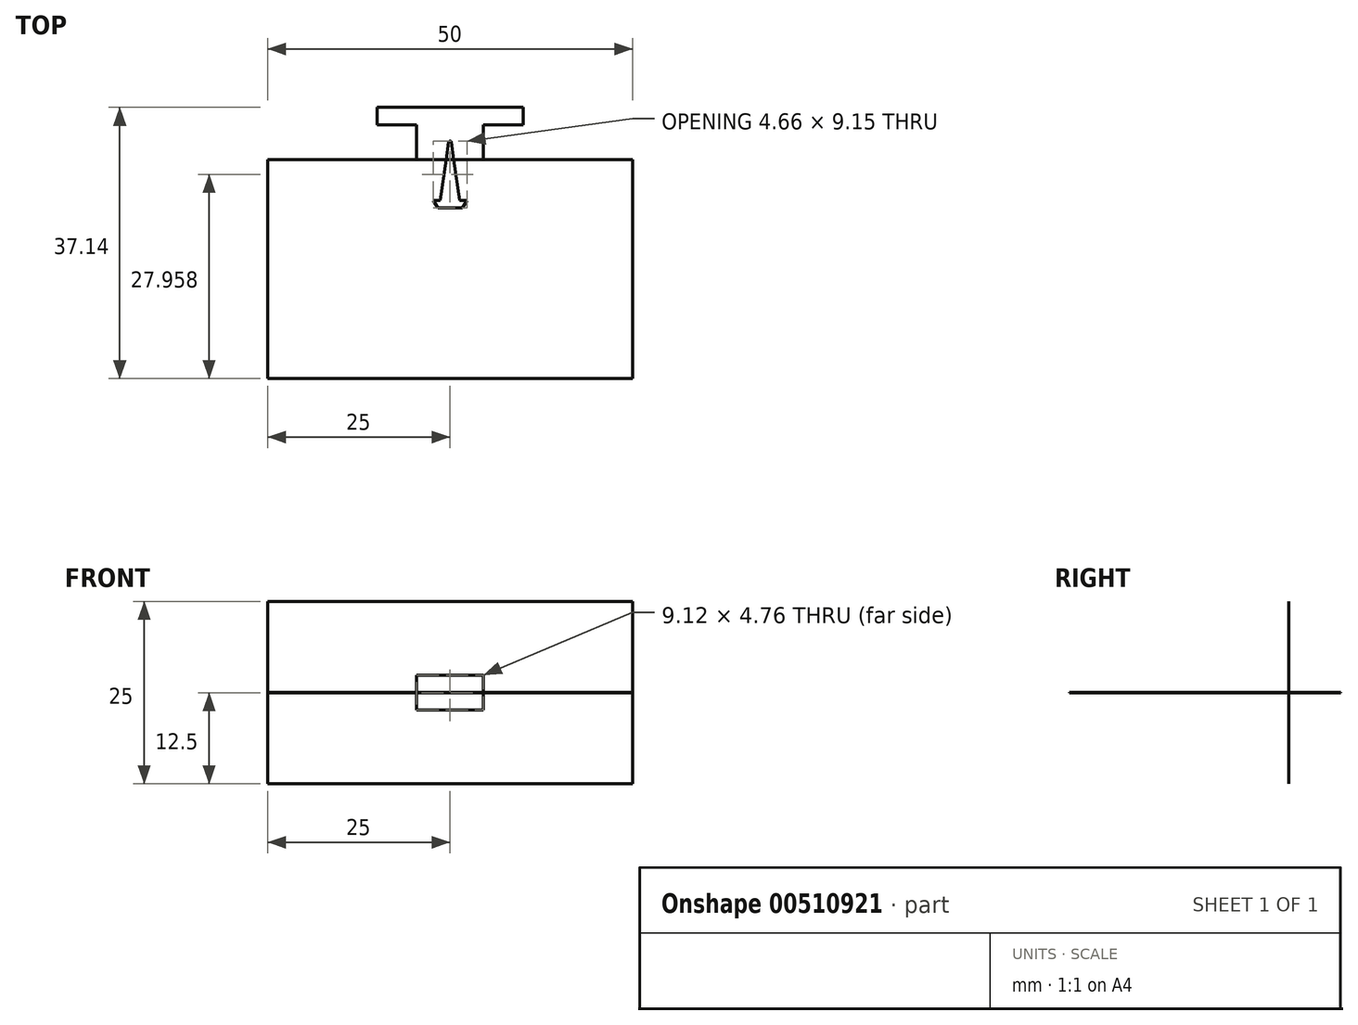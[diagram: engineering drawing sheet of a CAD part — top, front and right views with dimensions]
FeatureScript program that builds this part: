
annotation { "Feature Type Name" : "Feature", "Feature Type Description" : "" }
export const myFeature = defineFeature(function(context is Context, id is Id, definition is map)
    precondition{}
    {
        {
            assignVariable(context, id + "F0", {"name" : "thick", "anyValue" : 3 / 406.4 * mm});
        }
        {
            var Q0;
            Q0=qCreatedBy(makeId("Top.planeOp"),FACE);
            var sketch = newSketch(context, id + "F1", { "sketchPlane" : qUnion([Q0])});
            skLineSegment(sketch, "E0", {"start": v(0, 0) * mm, "end": v(0, -30) * mm, "construction": true});
            skLineSegment(sketch, "E1", {"start": v(-25, 0) * mm, "end": v(-4.56, 0) * mm});
            skLineSegment(sketch, "E2", {"start": v(-25, 0) * mm, "end": v(-25, -30) * mm});
            skLineSegment(sketch, "E3", {"start": v(-25, -30) * mm, "end": v(0, -30) * mm});
            skLineSegment(sketch, "E4.MirrorCS", {"start": v(25, -30) * mm, "end": v(0, -30) * mm});
            skLineSegment(sketch, "E5.MirrorCS", {"start": v(25, 0) * mm, "end": v(25, -30) * mm});
            skLineSegment(sketch, "E6.MirrorCS", {"start": v(25, 0) * mm, "end": v(4.56, 0) * mm});
            skLineSegment(sketch, "E7", {"start": v(4.56, 0) * mm, "end": v(4.56, 2.38) * mm});
            skLineSegment(sketch, "E8", {"start": v(4.56, 2.38) * mm, "end": v(2.18, 2.38) * mm});
            skLineSegment(sketch, "E9", {"start": v(2.18, 2.38) * mm, "end": v(2.18, -4.62) * mm});
            skLineSegment(sketch, "E10", {"start": v(2.18, -4.62) * mm, "end": v(2.98, -4.62) * mm});
            skLineSegment(sketch, "E11", {"start": v(2.98, -4.62) * mm, "end": v(1.68, -6.62) * mm});
            skLineSegment(sketch, "E12", {"start": v(1.68, -6.62) * mm, "end": v(1.68, -7.62) * mm, "construction": true});
            skLineSegment(sketch, "E13", {"start": v(1.68, -7.62) * mm, "end": v(0, -7.62) * mm, "construction": true});
            skLineSegment(sketch, "E14.MirrorCS", {"start": v(-2.18, -4.62) * mm, "end": v(-2.98, -4.62) * mm});
            skLineSegment(sketch, "E15.MirrorCS", {"start": v(-1.68, -6.62) * mm, "end": v(-1.68, -7.62) * mm, "construction": true});
            skLineSegment(sketch, "E16.MirrorCS", {"start": v(-4.56, 2.38) * mm, "end": v(-2.18, 2.38) * mm});
            skLineSegment(sketch, "E17.MirrorCS", {"start": v(-2.18, 2.38) * mm, "end": v(-2.18, -4.62) * mm});
            skLineSegment(sketch, "E18.MirrorCS", {"start": v(-4.56, 0) * mm, "end": v(-4.56, 2.38) * mm});
            skLineSegment(sketch, "E19.MirrorCS", {"start": v(-2.98, -4.62) * mm, "end": v(-1.68, -6.62) * mm});
            skLineSegment(sketch, "E20.MirrorCS", {"start": v(-1.68, -7.62) * mm, "end": v(0, -7.62) * mm, "construction": true});
            skLineSegment(sketch, "E21", {"start": v(1.68, -6.62) * mm, "end": v(-1.68, -6.62) * mm});
            skSolve(sketch);
        }
        {
            var Q0;
            Q0=makeQuery(id+"F1.imprint","IMPRINT",FACE,{"disambiguationData":[TD([[makeQuery(id+"F1.imprint","IMPRINT",EDGE,{"derivedFrom":sQuery(id+"F1.wireOp",EDGE,"E1")}),-1.0]])]});
            extrude(context, id + "F2", {"entities" : qUnion([Q0]), "endBound" : BoundingType.SYMMETRIC, "depth" : getVariable(context, 'thick')});
        }
        {
            var Q0;
            Q0=qCreatedBy(makeId("Front.planeOp"),FACE);
            var sketch = newSketch(context, id + "F3", { "sketchPlane" : qUnion([Q0])});
            skLineSegment(sketch, "E22.bottom", {"start": v(-25, 12.5) * mm, "end": v(25, 12.5) * mm});
            skLineSegment(sketch, "E22.top", {"start": v(-25, -12.5) * mm, "end": v(25, -12.5) * mm});
            skLineSegment(sketch, "E22.left", {"start": v(-25, 12.5) * mm, "end": v(-25, -12.5) * mm});
            skLineSegment(sketch, "E22.right", {"start": v(25, 12.5) * mm, "end": v(25, -12.5) * mm});
            skPoint(sketch, "E22.middle", {"position": v(0, 0) * mm});
            skLineSegment(sketch, "E23.bottom", {"start": v(4.56, 2.38) * mm, "end": v(-4.56, 2.38) * mm});
            skLineSegment(sketch, "E23.top", {"start": v(4.56, -2.38) * mm, "end": v(-4.56, -2.38) * mm});
            skLineSegment(sketch, "E23.left", {"start": v(4.56, 2.38) * mm, "end": v(4.56, -2.38) * mm});
            skLineSegment(sketch, "E23.right", {"start": v(-4.56, 2.38) * mm, "end": v(-4.56, -2.38) * mm});
            skSolve(sketch);
        }
        {
            var Q0;
            Q0=makeQuery(id+"F3.imprint","IMPRINT",FACE,{"disambiguationData":[TD([[makeQuery(id+"F3.imprint","IMPRINT",EDGE,{"derivedFrom":sQuery(id+"F3.wireOp",EDGE,"E22.bottom")}),-1.0]])]});
            extrude(context, id + "F4", {"entities" : qUnion([Q0]), "oppositeDirection" : true, "depth" : getVariable(context, 'thick')});
        }
        {
            var Q0;
            Q0=qCreatedBy(makeId("Top.planeOp"),FACE);
            var sketch = newSketch(context, id + "F5", { "sketchPlane" : qUnion([Q0])});
            skLineSegment(sketch, "E24", {"start": v(0, 7.14) * mm, "end": v(0, 0) * mm, "construction": true});
            skLineSegment(sketch, "E25.0", {"start": v(2.98, -4.62) * mm, "end": v(2.98, -4.62) * mm});
            skLineSegment(sketch, "E25.1", {"start": v(2.18, -4.62) * mm, "end": v(2.98, -4.62) * mm});
            skLineSegment(sketch, "E25.2", {"start": v(2.18, 2.38) * mm, "end": v(2.18, -4.62) * mm});
            skLineSegment(sketch, "E25.3", {"start": v(4.56, 2.38) * mm, "end": v(2.18, 2.38) * mm});
            skLineSegment(sketch, "E25.4", {"start": v(4.56, 4.76) * mm, "end": v(4.56, 0) * mm});
            skLineSegment(sketch, "E25.5", {"start": v(4.56, 4.76) * mm, "end": v(-4.56, 4.76) * mm, "construction": true});
            skLineSegment(sketch, "E26", {"start": v(2.98, -4.62) * mm, "end": v(2.33, -5.62) * mm});
            skLineSegment(sketch, "E27", {"start": v(1.5, -6.89) * mm, "end": v(1.44, -6.49) * mm});
            skLineSegment(sketch, "E28", {"start": v(2.18, 2.38) * mm, "end": v(1.18, 2.38) * mm, "construction": true});
            skLineSegment(sketch, "E29", {"start": v(1.18, 2.38) * mm, "end": v(0.18, 2.38) * mm, "construction": true});
            skLineSegment(sketch, "E30", {"start": v(2.18, -4.62) * mm, "end": v(1.18, -4.62) * mm, "construction": true});
            skArc(sketch, "E31", {"start": v(0.18, 2.38) * mm, "mid": v(0.12, 2.5) * mm, "end": v(0, 2.53) * mm});
            skLineSegment(sketch, "E32", {"start": v(4.56, 4.76) * mm, "end": v(10, 4.76) * mm});
            skLineSegment(sketch, "E33", {"start": v(10, 4.76) * mm, "end": v(10, 7.14) * mm});
            skLineSegment(sketch, "E34", {"start": v(10, 7.14) * mm, "end": v(0, 7.14) * mm});
            skArc(sketch, "E35", {"start": v(1.44, -6.49) * mm, "mid": v(1.56, -6.62) * mm, "end": v(1.72, -6.55) * mm});
            skLineSegment(sketch, "E36", {"start": v(0, 2.53) * mm, "end": v(0, 7.14) * mm});
            skLineSegment(sketch, "E37", {"start": v(2.33, -5.62) * mm, "end": v(1.32, -5.62) * mm});
            skLineSegment(sketch, "E38.trimOffspring", {"start": v(1.72, -6.55) * mm, "end": v(1.5, -6.89) * mm});
            skLineSegment(sketch, "E39.trimOffspring", {"start": v(1.32, -5.62) * mm, "end": v(0.18, 2.38) * mm});
            skSolve(sketch);
        }
        {
            var Q0;
            Q0=makeQuery(id+"F5.imprint","IMPRINT",FACE,{"disambiguationData":[TD([[makeQuery(id+"F5.imprint","IMPRINT",EDGE,{"derivedFrom":sQuery(id+"F5.wireOp",EDGE,"E25.1")}),-1.0]])]});
            extrude(context, id + "F6", {"entities" : qUnion([Q0]), "endBound" : BoundingType.SYMMETRIC, "depth" : getVariable(context, 'thick')});
        }
        {
            var Q0;
            Q0=makeQuery(id+"F6.opExtrude","SWEPT_BODY",BODY,{"disambiguationData":[OSD([sQuery(id+"F5.wireOp",EDGE,"E25.1"),sQuery(id+"F5.wireOp",EDGE,"E25.2"),sQuery(id+"F5.wireOp",EDGE,"E25.3"),sQuery(id+"F5.wireOp",EDGE,"E25.4"),sQuery(id+"F5.wireOp",EDGE,"E26"),sQuery(id+"F5.wireOp",EDGE,"E27"),sQuery(id+"F5.wireOp",EDGE,"E31"),sQuery(id+"F5.wireOp",EDGE,"E32"),sQuery(id+"F5.wireOp",EDGE,"E33"),sQuery(id+"F5.wireOp",EDGE,"E34"),sQuery(id+"F5.wireOp",EDGE,"E35"),sQuery(id+"F5.wireOp",EDGE,"E36")])]});
            var Q1;
            Q1=makeQuery(id+"F6.opExtrude","SWEPT_FACE",FACE,{"disambiguationData":[OSD([sQuery(id+"F5.wireOp",EDGE,"E36")])]});
            mirror(context, id + "F7", {"operationType" : NewBodyOperationType.ADD, "entities" : qUnion([Q0]), "mirrorPlane" : qUnion([Q1])});
        }
    });
